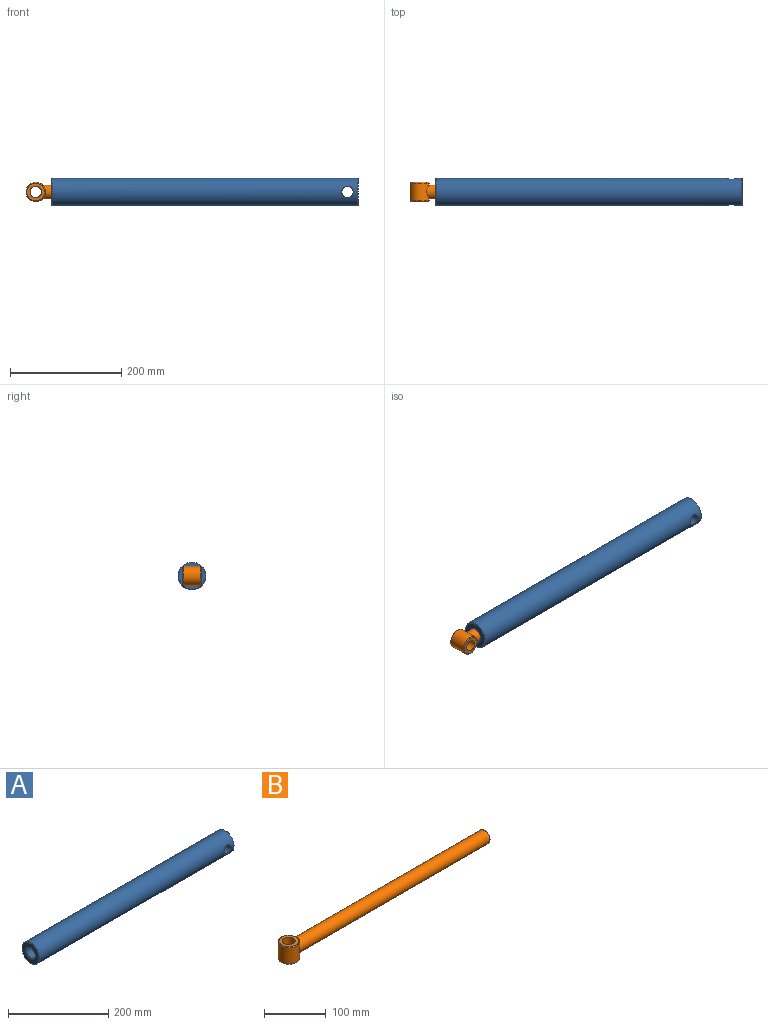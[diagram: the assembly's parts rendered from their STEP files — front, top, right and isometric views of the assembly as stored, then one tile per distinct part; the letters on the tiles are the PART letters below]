
ASSEMBLY  parts=2 mates=1
PART A: 9 faces, bbox 551.5x50x50 mm
  f0: cylinder r=25mm len=549.5mm, axis (-1,0,0), area 85640.1mm2, adj f5,f7,f8
  f1: plane 48x48mm, normal (1,0,0), area 1809.6mm2, adj f5
  f2: plane 48x48mm, normal (-1,0,0), area 1237mm2, adj f6,f7
  f3: cone r=0mm half-angle=59deg, axis (-1,0,0), area 572.7mm2, adj f4
  f4: cylinder r=12.5mm len=499mm, axis (-1,0,0), area 39191.4mm2, adj f3,f6
  f5: cone r=24mm half-angle=45deg, axis (-1,0,0), area 217.7mm2, adj f0,f1
  f6: cone r=12.5mm half-angle=45deg, axis (-1,0,0), area 115.5mm2, adj f2,f4
  f7: cone r=25mm half-angle=45deg, axis (1,0,0), area 217.7mm2, adj f0,f2
  f8: cylinder r=10.25mm len=50mm, axis (0,1,0), area 3080.3mm2, adj f0
PART B: 8 faces, bbox 467.5x35x35 mm
  f0: cylinder r=12.5mm len=437.75mm, axis (-1,0,0), area 34165.6mm2, adj f1,f2
  f1: plane 25x25mm, normal (1,0,0), area 490.9mm2, adj f0
  f2: cylinder r=17.5mm len=35mm, axis (0,0,-1), area 2988.6mm2, adj f0,f5,f6
  f3: plane 32x32mm, normal (0,0,1), area 474.2mm2, adj f6,f7
  f4: plane 32x32mm, normal (0,0,-1), area 474.2mm2, adj f5,f7
  f5: cone r=17.5mm half-angle=45deg, axis (0,0,1), area 223.3mm2, adj f2,f4
  f6: cone r=16mm half-angle=45deg, axis (0,0,-1), area 223.3mm2, adj f2,f3
  f7: cylinder r=10.25mm len=35mm, axis (0,0,1), area 2254.1mm2, adj f3,f4
PLACE A at identity fixed
PLACE B rot(axis=(-1,0,0),90deg) t=(-28.79,0,0)mm
MATE cylindrical B.f0 <-> A.f0  axis (-1,0,0) through (201,0,0)mm
